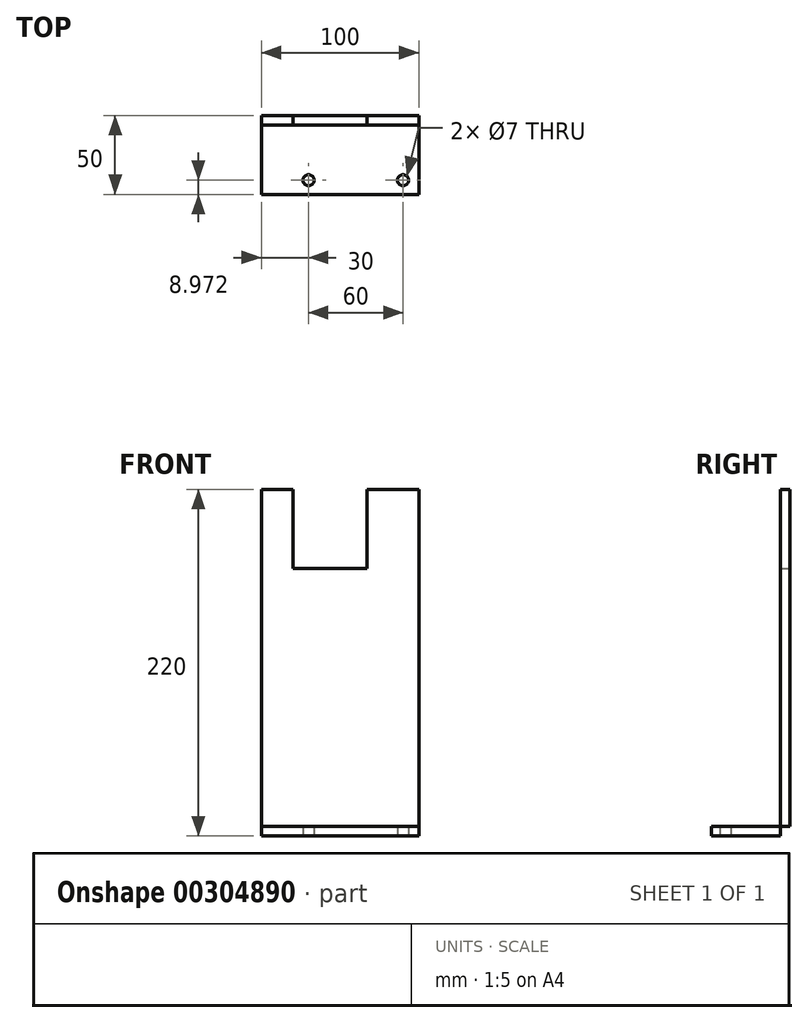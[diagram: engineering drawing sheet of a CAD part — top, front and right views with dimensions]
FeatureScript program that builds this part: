
annotation { "Feature Type Name" : "Feature", "Feature Type Description" : "" }
export const myFeature = defineFeature(function(context is Context, id is Id, definition is map)
    precondition{}
    {
        {
            var Q0;
            Q0=qCreatedBy(makeId("Right.planeOp"),FACE);
            var sketch = newSketch(context, id + "F0", { "sketchPlane" : qUnion([Q0])});
            skLineSegment(sketch, "E0.bottom", {"start": v(0, 0) * mm, "end": v(-6, 0) * mm});
            skLineSegment(sketch, "E0.top", {"start": v(0, 220) * mm, "end": v(-6, 220) * mm});
            skLineSegment(sketch, "E0.left", {"start": v(0, 0) * mm, "end": v(0, 220) * mm});
            skLineSegment(sketch, "E0.right", {"start": v(-6, 0) * mm, "end": v(-6, 220) * mm});
            skLineSegment(sketch, "E1.bottom", {"start": v(0, 0) * mm, "end": v(-50, 0) * mm});
            skLineSegment(sketch, "E1.top", {"start": v(0, 6) * mm, "end": v(-50, 6) * mm});
            skLineSegment(sketch, "E1.left", {"start": v(0, 0) * mm, "end": v(0, 6) * mm});
            skLineSegment(sketch, "E1.right", {"start": v(-50, 0) * mm, "end": v(-50, 6) * mm});
            skSolve(sketch);
        }
        {
            var Q0;
            {var subQ0=sQuery(id+"F0.wireOp",EDGE,"E0.top");Q0=makeQuery(id+"F0.imprint","IMPRINT",FACE,{"disambiguationData":[TD([[makeQuery(id+"F0.imprint","IMPRINT",EDGE,{"derivedFrom":subQ0}),1.0]])]});}
            var Q1;
            {var subQ5=sQuery(id+"F0.wireOp",EDGE,"E1.left");Q1=makeQuery(id+"F0.imprint","IMPRINT",FACE,{"disambiguationData":[TD([[makeQuery(id+"F0.imprint","IMPRINT",EDGE,{"derivedFrom":subQ5}),1.0]])]});}
            var Q2;
            {var subQ5=sQuery(id+"F0.wireOp",EDGE,"E1.right");Q2=makeQuery(id+"F0.imprint","IMPRINT",FACE,{"disambiguationData":[TD([[makeQuery(id+"F0.imprint","IMPRINT",EDGE,{"derivedFrom":subQ5}),-1.0]])]});}
            extrude(context, id + "F1", {"entities" : qUnion([Q0, Q1, Q2]), "depth" : 100 * mm});
        }
        {
            var Q0;
            Q0=qCreatedBy(makeId("Top.planeOp"),FACE);
            var sketch = newSketch(context, id + "F2", { "sketchPlane" : qUnion([Q0])});
            skLineSegment(sketch, "E2", {"start": v(30, 0) * mm, "end": v(30, -50.46) * mm, "construction": true});
            skLineSegment(sketch, "E3", {"start": v(90, 0) * mm, "end": v(90, -50.33) * mm, "construction": true});
            skLineSegment(sketch, "E4", {"start": v(0, -41.03) * mm, "end": v(100, -41.03) * mm, "construction": true});
            skCircle(sketch, "E5", {"center": v(30, -41.03) * mm, "radius": 3.5 * mm});
            skCircle(sketch, "E6", {"center": v(90, -41.03) * mm, "radius": 3.5 * mm});
            skSolve(sketch);
        }
        {
            var Q0;
            Q0=sQuery(id+"F2.wireOp",VERTEX,"E5.center");
            var Q1;
            Q1=sQuery(id+"F2.wireOp",VERTEX,"E6.center");
            var Q2;
            Q2=makeQuery(id+"F1.opExtrude","SWEPT_BODY",BODY,{"disambiguationData":[OSD([sQuery(id+"F0.wireOp",EDGE,"E0.top"),sQuery(id+"F0.wireOp",EDGE,"E0.left"),sQuery(id+"F0.wireOp",EDGE,"E0.right"),sQuery(id+"F0.wireOp",EDGE,"E1.bottom"),sQuery(id+"F0.wireOp",EDGE,"E1.top"),sQuery(id+"F0.wireOp",EDGE,"E1.left"),sQuery(id+"F0.wireOp",EDGE,"E1.right")])]});
            hole(context, id + "F3", {"style" : HoleStyle.SIMPLE, "endStyle" : HoleEndStyle.THROUGH, "oppositeDirection" : true, "holeDiameter" : 7 * mm, "tappedDepth" : 12 * mm, "tapClearance" : 3, "locations" : qUnion([Q0, Q1]), "scope" : qUnion([Q2])});
        }
        {
            var Q0;
            Q0=qCreatedBy(makeId("Front.planeOp"),FACE);
            var sketch = newSketch(context, id + "F4", { "sketchPlane" : qUnion([Q0])});
            skLineSegment(sketch, "E7", {"start": v(20, 220) * mm, "end": v(20, 170) * mm});
            skLineSegment(sketch, "E8", {"start": v(20, 170) * mm, "end": v(67, 170) * mm});
            skLineSegment(sketch, "E9", {"start": v(67, 170) * mm, "end": v(67, 220) * mm});
            skLineSegment(sketch, "E10", {"start": v(67, 220) * mm, "end": v(20, 220) * mm});
            skSolve(sketch);
        }
        {
            var Q0;
            Q0=makeQuery(id+"F4.imprint","IMPRINT",FACE,{"disambiguationData":[TD([[makeQuery(id+"F4.imprint","IMPRINT",EDGE,{"derivedFrom":sQuery(id+"F4.wireOp",EDGE,"E7")}),1.0]])]});
            extrude(context, id + "F5", {"entities" : qUnion([Q0]), "operationType" : NewBodyOperationType.REMOVE, "depth" : 25 * mm});
        }
        {
            var Q0;
            Q0=makeQuery(id+"F1.opExtrude","SWEPT_BODY",BODY,{"disambiguationData":[OSD([sQuery(id+"F0.wireOp",EDGE,"E0.top"),sQuery(id+"F0.wireOp",EDGE,"E0.left"),sQuery(id+"F0.wireOp",EDGE,"E0.right"),sQuery(id+"F0.wireOp",EDGE,"E1.bottom"),sQuery(id+"F0.wireOp",EDGE,"E1.top"),sQuery(id+"F0.wireOp",EDGE,"E1.left"),sQuery(id+"F0.wireOp",EDGE,"E1.right")])]});
            var Q1;
            Q1=qCreatedBy(makeId("Front.planeOp"),FACE);
            mirror(context, id + "F6", {"entities" : qUnion([Q0]), "mirrorPlane" : qUnion([Q1])});
        }
        {
            var Q0;
            Q0=makeQuery(id+"F6.opPattern","COPY",BODY,{"derivedFrom":makeQuery(id+"F1.opExtrude","SWEPT_BODY",BODY,{"disambiguationData":[OSD([sQuery(id+"F0.wireOp",EDGE,"E0.top"),sQuery(id+"F0.wireOp",EDGE,"E0.left"),sQuery(id+"F0.wireOp",EDGE,"E0.right"),sQuery(id+"F0.wireOp",EDGE,"E1.bottom"),sQuery(id+"F0.wireOp",EDGE,"E1.top"),sQuery(id+"F0.wireOp",EDGE,"E1.left"),sQuery(id+"F0.wireOp",EDGE,"E1.right")])]}),"instanceName":"1"});
            deleteBodies(context, id + "F7", {"entities" : qUnion([Q0])});
        }
    });
